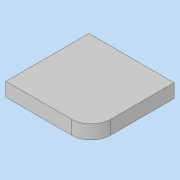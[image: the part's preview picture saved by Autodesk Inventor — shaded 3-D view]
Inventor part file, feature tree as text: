
AUTODESK INVENTOR PART (.ipt)
format: ipt  version: 2019 (Build 230136000, 136)  size: 88,576 bytes
history: native  units: mm
features: sketch x3, other x1, extrude x1, fillet x1
ambient origin geometry x8: Origin, YZ Plane, XZ Plane, XY Plane, X Axis, Y Axis, Z Axis, Center Point
bodies: Body1 (feature_tree)
feature tree (6):
  other  "Твердое тело1"
  extrude  "Выдавливание1"  Depth=185.0mm
  fillet  "Сопряжение1"  Radius=180.0mm
  sketch  "Эскиз1"
  sketch  "Эскиз3"
  sketch  "Эскиз4"
